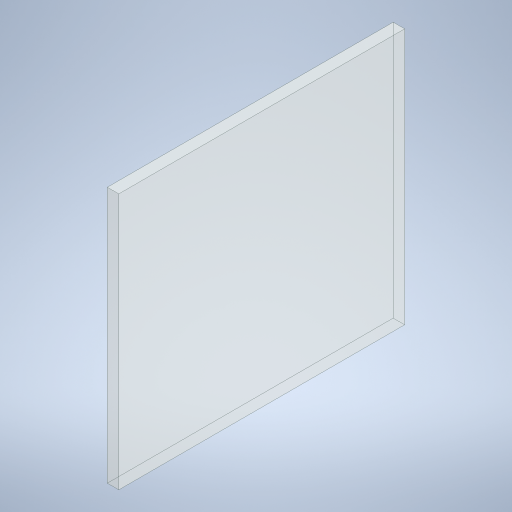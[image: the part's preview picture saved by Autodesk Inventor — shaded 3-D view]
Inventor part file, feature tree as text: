
AUTODESK INVENTOR PART (.ipt)
format: ipt  version: 2024 (Build 280153000, 153)  size: 218,624 bytes
history: native  units: in
note: dims shown in document units (in); Inventor stores cm internally (conversion verified against a paired STEP export)
features: extrude x1, sketch x1
ambient origin geometry x8: Origin, YZ Plane, XZ Plane, XY Plane, X Axis, Y Axis, Z Axis, Center Point
bodies: Solid1 (feature_tree)
feature tree (2):
  extrude  "Extrusion1"  Depth=78.0in
  sketch  "Sketch1"  dims[d2=87.0in d3=78.0in d4=3.5in d5=0.0in]
